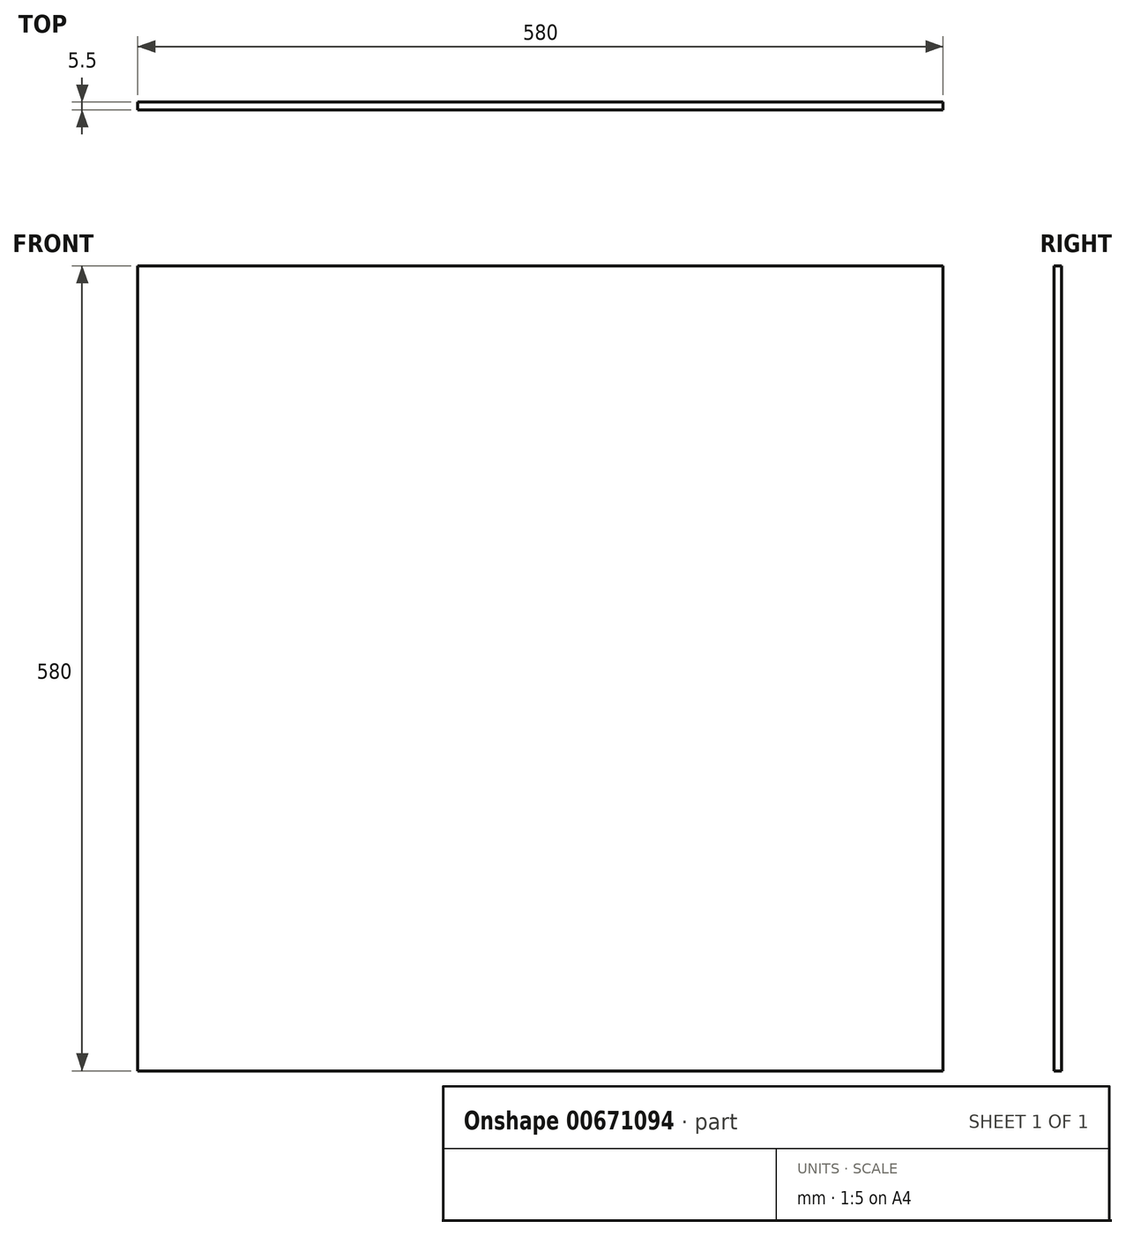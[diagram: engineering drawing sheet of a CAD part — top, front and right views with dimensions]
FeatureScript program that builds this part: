
annotation { "Feature Type Name" : "Feature", "Feature Type Description" : "" }
export const myFeature = defineFeature(function(context is Context, id is Id, definition is map)
    precondition{}
    {
        {
            var Q0;
            Q0=qCreatedBy(makeId("Front.planeOp"),FACE);
            var sketch = newSketch(context, id + "F0", { "sketchPlane" : qUnion([Q0])});
            skLineSegment(sketch, "E0.bottom", {"start": v(580, 580) * mm, "end": v(0, 580) * mm});
            skLineSegment(sketch, "E0.top", {"start": v(580, 0) * mm, "end": v(0, 0) * mm});
            skLineSegment(sketch, "E0.left", {"start": v(580, 580) * mm, "end": v(580, 0) * mm});
            skLineSegment(sketch, "E0.right", {"start": v(0, 580) * mm, "end": v(0, 0) * mm});
            skSolve(sketch);
        }
        {
            var Q0;
            Q0=makeQuery(id+"F0.imprint","IMPRINT",FACE,{"disambiguationData":[TD([[makeQuery(id+"F0.imprint","IMPRINT",EDGE,{"derivedFrom":sQuery(id+"F0.wireOp",EDGE,"E0.bottom")}),1.0]])]});
            extrude(context, id + "F1", {"entities" : qUnion([Q0]), "depth" : 5.5 * mm, "offsetDistance" : 25 * mm});
        }
    });
